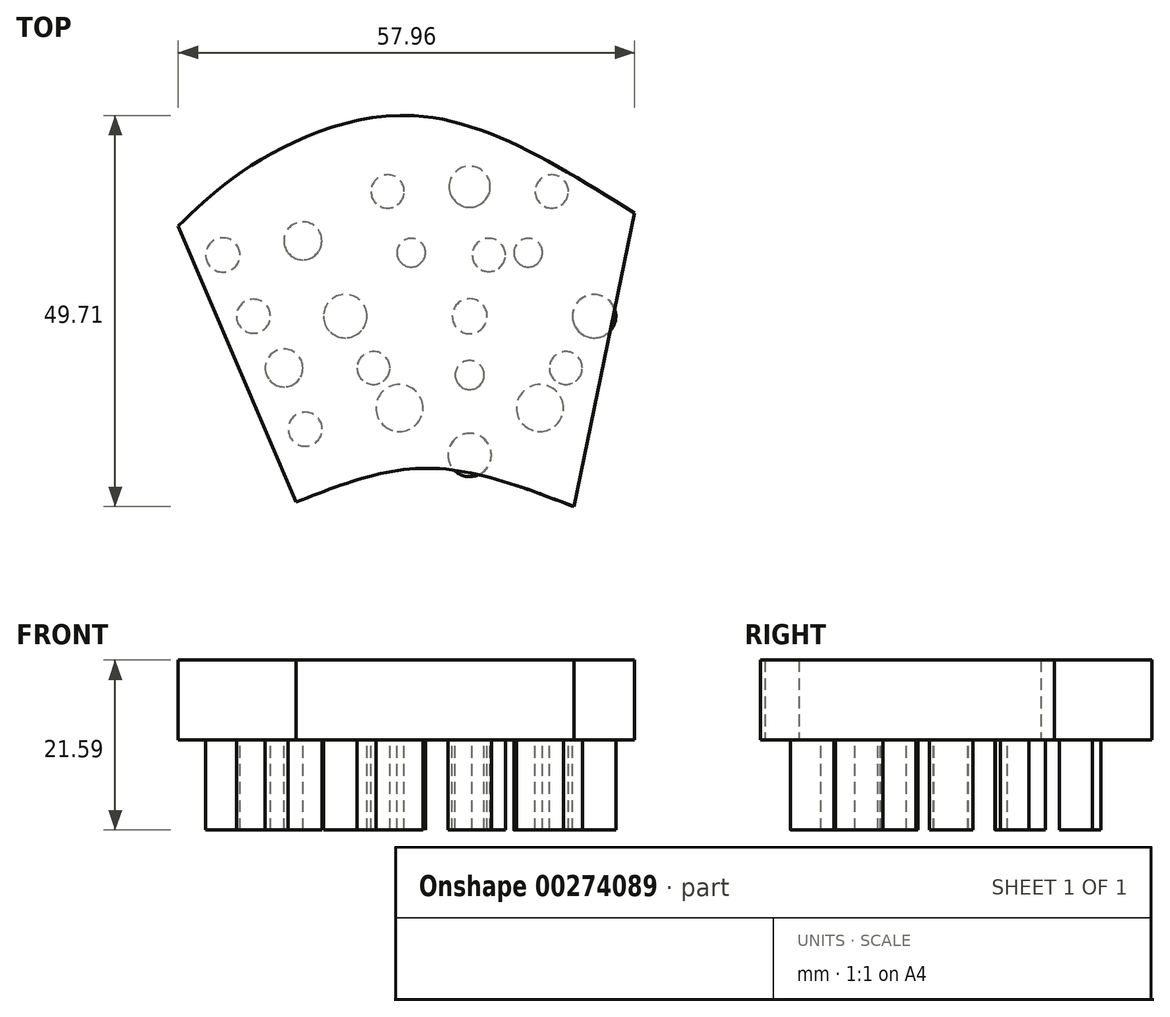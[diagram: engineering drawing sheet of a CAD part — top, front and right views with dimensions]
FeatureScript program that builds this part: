
annotation { "Feature Type Name" : "Feature", "Feature Type Description" : "" }
export const myFeature = defineFeature(function(context is Context, id is Id, definition is map)
    precondition{}
    {
        {
            var Q0;
            Q0=qCreatedBy(makeId("Top.planeOp"),FACE);
            var sketch = newSketch(context, id + "F0", { "sketchPlane" : qUnion([Q0])});
            skFitSpline(sketch, "E0", {"points": [v(-22.07, -6) * mm, v(-5.41, -1.69) * mm, v(13.26, -6.57) * mm], "startDerivative": vector(33.82, 13.33) * mm, "endDerivative": vector(36.82, -14.22) * mm});
            skLineSegment(sketch, "E1", {"start": v(-22.07, -6) * mm, "end": v(-37.01, 29.05) * mm});
            skLineSegment(sketch, "E2", {"start": v(13.26, -6.57) * mm, "end": v(20.95, 30.74) * mm});
            skFitSpline(sketch, "E3", {"points": [v(-37.01, 29.05) * mm, v(-28.17, 36.48) * mm, v(-7.1, 43.1) * mm, v(20.95, 30.74) * mm], "startDerivative": vector(30.12, 29.65) * mm, "endDerivative": vector(69.5, -42.94) * mm});
            skLineSegment(sketch, "E4", {"start": v(-7.1, 43.1) * mm, "end": v(-5.41, -1.69) * mm});
            skPoint(sketch, "E5", {"position": v(-6.43, 25.43) * mm});
            skSolve(sketch);
        }
        {
            var Q0;
            Q0=makeQuery(id+"F0.imprint","IMPRINT",FACE,{"disambiguationData":[TD([[makeQuery(id+"F0.imprint","IMPRINT",EDGE,{"derivedFrom":sQuery(id+"F0.wireOp",EDGE,"E0")}),1.0]])]});
            extrude(context, id + "F1", {"entities" : qUnion([Q0]), "depth" : 10.16 * mm});
        }
        {
            var Q0;
            Q0=makeQuery(id+"F1.opExtrude","CAP_FACE",FACE,{"disambiguationData":[OSD([sQuery(id+"F0.wireOp",EDGE,"E0"),sQuery(id+"F0.wireOp",EDGE,"E1"),sQuery(id+"F0.wireOp",EDGE,"E2"),sQuery(id+"F0.wireOp",EDGE,"E3")])],"isStart":true});
            var sketch = newSketch(context, id + "F2", { "sketchPlane" : qUnion([Q0])});
            skCircle(sketch, "E6", {"center": v(-20.89, -3.27) * mm, "radius": 2.16 * mm});
            skCircle(sketch, "E7", {"center": v(-23.58, -11.05) * mm, "radius": 2.4 * mm});
            skCircle(sketch, "E8", {"center": v(-27.47, -17.63) * mm, "radius": 2.16 * mm});
            skCircle(sketch, "E9", {"center": v(-31.36, -25.4) * mm, "radius": 2.18 * mm});
            skCircle(sketch, "E10", {"center": v(-21.19, -27.2) * mm, "radius": 2.41 * mm});
            skCircle(sketch, "E11", {"center": v(-15.8, -17.63) * mm, "radius": 2.76 * mm});
            skCircle(sketch, "E12", {"center": v(-12.22, -11.05) * mm, "radius": 2.1 * mm});
            skCircle(sketch, "E13", {"center": v(-8.93, -5.96) * mm, "radius": 3 * mm});
            skCircle(sketch, "E14", {"center": v(0, -17.63) * mm, "radius": 2.22 * mm});
            skCircle(sketch, "E15", {"center": v(-7.43, -25.7) * mm, "radius": 1.82 * mm});
            skCircle(sketch, "E16", {"center": v(0, -10.15) * mm, "radius": 1.84 * mm});
            skCircle(sketch, "E17", {"center": v(-10.42, -33.48) * mm, "radius": 2.11 * mm});
            skCircle(sketch, "E18", {"center": v(2.44, -25.4) * mm, "radius": 2.11 * mm});
            skCircle(sketch, "E19", {"center": v(0, -34.07) * mm, "radius": 2.6 * mm});
            skCircle(sketch, "E20", {"center": v(0, 0) * mm, "radius": 2.75 * mm});
            skCircle(sketch, "E21.MirrorC", {"center": v(8.93, -5.96) * mm, "radius": 3 * mm});
            skCircle(sketch, "E22.MirrorC", {"center": v(12.22, -11.05) * mm, "radius": 2.1 * mm});
            skCircle(sketch, "E23.MirrorC", {"center": v(15.8, -17.63) * mm, "radius": 2.76 * mm});
            skCircle(sketch, "E24.MirrorC", {"center": v(10.42, -33.48) * mm, "radius": 2.11 * mm});
            skCircle(sketch, "E25.MirrorC", {"center": v(7.43, -25.7) * mm, "radius": 1.82 * mm});
            skSolve(sketch);
        }
        {
            var Q0;
            Q0 = qSketchRegion(id + "F2", true);
            extrude(context, id + "F3", {"entities" : qUnion([Q0]), "operationType" : NewBodyOperationType.ADD, "depth" : 11.43 * mm});
        }
    });
